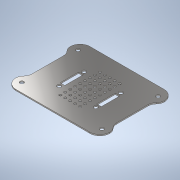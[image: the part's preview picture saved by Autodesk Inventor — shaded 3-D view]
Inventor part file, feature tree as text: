
AUTODESK INVENTOR PART (.ipt)
format: ipt  version: 2022 (Build 260153000, 153)  size: 252,416 bytes
history: native  units: in
note: dims shown in document units (in); Inventor stores cm internally (conversion verified against a paired STEP export)
features: sketch x6, extrude x3, hole x3
ambient origin geometry x8: Origin, YZ Plane, XZ Plane, XY Plane, X Axis, Y Axis, Z Axis, Center Point
bodies: Solid1 (feature_tree)
feature tree (12):
  extrude  "Extrusion1"  Depth=1.875in
  hole  "Hole1"  [1 undecoded]
  extrude  "Extrusion2"  Depth=0.47in
  hole  "Hole2"  [1 undecoded]
  extrude  "Extrusion3"  Depth=0.25in
  hole  "Hole3"  [1 undecoded]
  sketch  "Sketch1"  dims[d0=1.875in d1=2.375in]
  sketch  "Sketch2"  dims[d2=0.25in d3=0.0293in d4=0.0in]
  sketch  "Sketch3"  dims[d9=0.0984in d10=0.75in d11=0.119in d12=0.25in d13=0.5635in d14=1.0in d15=0.8108in d18=0.47in]
  sketch  "Sketch4"  dims[d19=0.0in d20=0.0in d21=0.1181in]
  sketch  "Sketch5"  dims[d24=0.5in d25=0.25in]
  sketch  "Sketch6"  dims[d26=3.5433in d28=0.125in d29=1.9685in d31=0.125in d34=0.0625in d35=0.75in d36=0.375in d37=0.25in d38=0.5635in d39=1.0in d40=0.8108in d41=0.2in d42=45.0deg d43=0.2in d44=45.0deg d45=0.2in d46=45.0deg d47=0.2in d48=45.0deg d49=1.0in d50=0.0in d51=0.2in d52=45.0deg d53=0.2in d54=45.0deg d57=0.2in d58=45.0deg d59=0.2in d60=45.0deg d61=0.315in d62=0.315in d65=0.1in d66=0.094in d67=0.375in d68=0.25in d69=0.5635in d70=1.0in d71=0.8108in d72=0.9264in d73=0.4632in d74=0.9264in d75=0.4632in d76=2.0276in d77=1.4213in d78=0.7106in d79=1.0138in]
note: 3 required parameter values undecoded (feature->parameter linkage not recoverable at this tier; creation-order binding heuristic only, values carry confidence <= 0.55)
